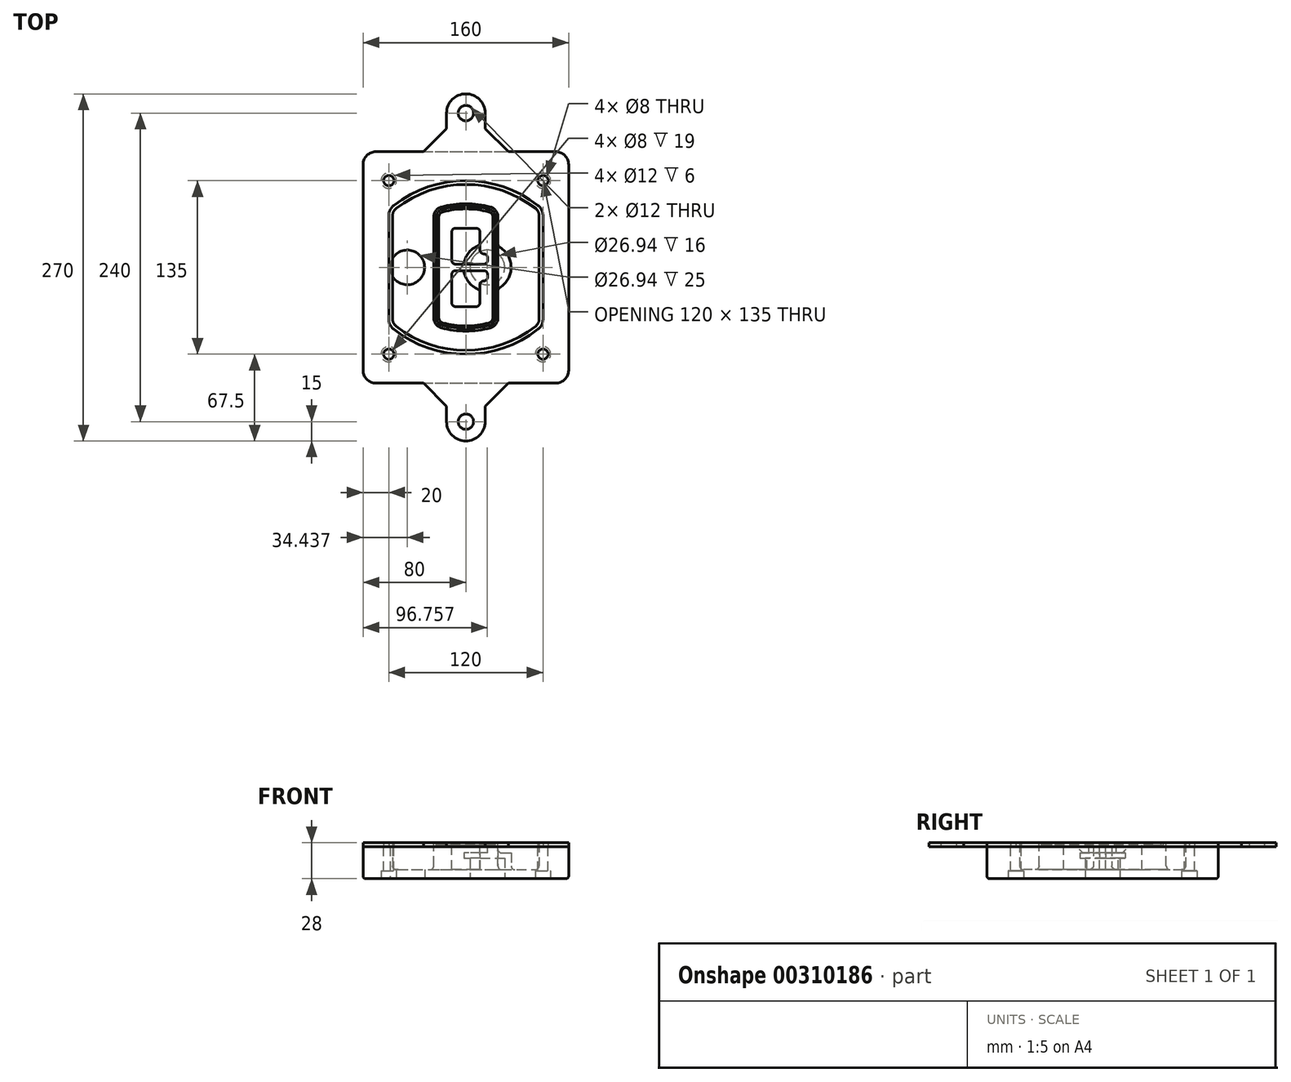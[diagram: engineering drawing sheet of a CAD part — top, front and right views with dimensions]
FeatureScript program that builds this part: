
annotation { "Feature Type Name" : "Feature", "Feature Type Description" : "" }
export const myFeature = defineFeature(function(context is Context, id is Id, definition is map)
    precondition{}
    {
        {
            var Q0;
            Q0=qCreatedBy(makeId("Top.planeOp"),FACE);
            var sketch = newSketch(context, id + "F0", { "sketchPlane" : qUnion([Q0])});
            skPoint(sketch, "E0.rect.middle", {"position": v(0, 0) * mm});
            skLineSegment(sketch, "E1.bottom", {"start": v(-70, -90) * mm, "end": v(70, -90) * mm});
            skLineSegment(sketch, "E1.top", {"start": v(-70, 90) * mm, "end": v(70, 90) * mm});
            skLineSegment(sketch, "E1.left", {"start": v(-80, -80) * mm, "end": v(-80, 80) * mm});
            skLineSegment(sketch, "E1.right", {"start": v(80, -80) * mm, "end": v(80, 80) * mm});
            skLineSegment(sketch, "E2", {"start": v(-80, 90) * mm, "end": v(80, -90) * mm, "construction": true});
            skLineSegment(sketch, "E3", {"start": v(80, 90) * mm, "end": v(-80, -90) * mm, "construction": true});
            skCircle(sketch, "E4", {"center": v(-60, 67.5) * mm, "radius": 4 * mm});
            skCircle(sketch, "E5", {"center": v(60, 67.5) * mm, "radius": 4 * mm});
            skCircle(sketch, "E6", {"center": v(60, -67.5) * mm, "radius": 4 * mm});
            skCircle(sketch, "E7", {"center": v(-60, -67.5) * mm, "radius": 4 * mm});
            skLineSegment(sketch, "E8", {"start": v(-60, 67.5) * mm, "end": v(60, 67.5) * mm, "construction": true});
            skLineSegment(sketch, "E9", {"start": v(60, 67.5) * mm, "end": v(60, -67.5) * mm, "construction": true});
            skLineSegment(sketch, "E10", {"start": v(60, -67.5) * mm, "end": v(-60, -67.5) * mm, "construction": true});
            skLineSegment(sketch, "E11", {"start": v(-60, -67.5) * mm, "end": v(-60, 67.5) * mm, "construction": true});
            skLineSegment(sketch, "E12", {"start": v(-60, 40.3) * mm, "end": v(-60, -40.3) * mm});
            skLineSegment(sketch, "E13", {"start": v(60, 40.3) * mm, "end": v(60, -40.3) * mm});
            skArc(sketch, "E14", {"start": v(56.15, 48.18) * mm, "mid": v(0, 67.5) * mm, "end": v(-56.15, 48.18) * mm});
            skArc(sketch, "E15", {"start": v(-56.15, -48.18) * mm, "mid": v(0, -67.5) * mm, "end": v(56.15, -48.18) * mm});
            skLineSegment(sketch, "E16", {"start": v(-60, 0) * mm, "end": v(60, 0) * mm, "construction": true});
            skPoint(sketch, "E17.visualSharp", {"position": v(-60, -45) * mm});
            skArc(sketch, "E17.filletArc", {"start": v(-60, -40.3) * mm, "mid": v(-58.99, -44.68) * mm, "end": v(-56.15, -48.18) * mm});
            skPoint(sketch, "E18.visualSharp", {"position": v(-60, 45) * mm});
            skArc(sketch, "E18.filletArc", {"start": v(-56.15, 48.18) * mm, "mid": v(-58.99, 44.68) * mm, "end": v(-60, 40.3) * mm});
            skPoint(sketch, "E19.visualSharp", {"position": v(60, 45) * mm});
            skArc(sketch, "E19.filletArc", {"start": v(60, 40.3) * mm, "mid": v(58.99, 44.68) * mm, "end": v(56.15, 48.18) * mm});
            skPoint(sketch, "E20.visualSharp", {"position": v(60, -45) * mm});
            skArc(sketch, "E20.filletArc", {"start": v(56.15, -48.18) * mm, "mid": v(58.99, -44.68) * mm, "end": v(60, -40.3) * mm});
            skPoint(sketch, "E21.visualSharp", {"position": v(-80, 90) * mm});
            skArc(sketch, "E21.filletArc", {"start": v(-70, 90) * mm, "mid": v(-77.07, 87.07) * mm, "end": v(-80, 80) * mm});
            skPoint(sketch, "E22.visualSharp", {"position": v(80, 90) * mm});
            skArc(sketch, "E22.filletArc", {"start": v(80, 80) * mm, "mid": v(77.07, 87.07) * mm, "end": v(70, 90) * mm});
            skPoint(sketch, "E23.visualSharp", {"position": v(80, -90) * mm});
            skArc(sketch, "E23.filletArc", {"start": v(70, -90) * mm, "mid": v(77.07, -87.07) * mm, "end": v(80, -80) * mm});
            skPoint(sketch, "E24.visualSharp", {"position": v(-80, -90) * mm});
            skArc(sketch, "E24.filletArc", {"start": v(-80, -80) * mm, "mid": v(-77.07, -87.07) * mm, "end": v(-70, -90) * mm});
            skArc(sketch, "E25.0", {"start": v(57, 40.3) * mm, "mid": v(56.3, 43.36) * mm, "end": v(54.3, 45.81) * mm});
            skLineSegment(sketch, "E25.1", {"start": v(57, 40.3) * mm, "end": v(57, -40.3) * mm});
            skArc(sketch, "E25.2", {"start": v(54.3, -45.81) * mm, "mid": v(56.3, -43.36) * mm, "end": v(57, -40.3) * mm});
            skArc(sketch, "E25.3", {"start": v(-54.3, -45.81) * mm, "mid": v(0, -64.5) * mm, "end": v(54.3, -45.81) * mm});
            skArc(sketch, "E25.4", {"start": v(-57, -40.3) * mm, "mid": v(-56.3, -43.36) * mm, "end": v(-54.3, -45.81) * mm});
            skArc(sketch, "E25.5", {"start": v(54.3, 45.81) * mm, "mid": v(0, 64.5) * mm, "end": v(-54.3, 45.81) * mm});
            skLineSegment(sketch, "E25.6", {"start": v(-57, 40.3) * mm, "end": v(-57, -40.3) * mm});
            skArc(sketch, "E25.7", {"start": v(-54.3, 45.81) * mm, "mid": v(-56.3, 43.36) * mm, "end": v(-57, 40.3) * mm});
            skArc(sketch, "E26.0", {"start": v(-58.62, 51.33) * mm, "mid": v(-62.58, 46.43) * mm, "end": v(-64, 40.3) * mm});
            skArc(sketch, "E26.1", {"start": v(58.62, 51.33) * mm, "mid": v(0, 71.5) * mm, "end": v(-58.62, 51.33) * mm});
            skArc(sketch, "E26.2", {"start": v(64, 40.3) * mm, "mid": v(62.58, 46.43) * mm, "end": v(58.62, 51.33) * mm});
            skLineSegment(sketch, "E26.3", {"start": v(64, 40.3) * mm, "end": v(64, -40.3) * mm});
            skArc(sketch, "E26.4", {"start": v(58.62, -51.33) * mm, "mid": v(62.58, -46.43) * mm, "end": v(64, -40.3) * mm});
            skLineSegment(sketch, "E26.5", {"start": v(-64, 40.3) * mm, "end": v(-64, -40.3) * mm});
            skArc(sketch, "E26.6", {"start": v(-58.62, -51.33) * mm, "mid": v(0, -71.5) * mm, "end": v(58.62, -51.33) * mm});
            skArc(sketch, "E26.7", {"start": v(-64, -40.3) * mm, "mid": v(-62.58, -46.43) * mm, "end": v(-58.62, -51.33) * mm});
            skSolve(sketch);
        }
        {
            var Q0;
            Q0=makeQuery(id+"F0.imprint","IMPRINT",FACE,{"disambiguationData":[TD([[makeQuery(id+"F0.imprint","IMPRINT",EDGE,{"derivedFrom":sQuery(id+"F0.wireOp",EDGE,"E1.bottom")}),1.0]])]});
            var Q1;
            Q1=makeQuery(id+"F0.imprint","IMPRINT",FACE,{"disambiguationData":[TD([[makeQuery(id+"F0.imprint","IMPRINT",EDGE,{"derivedFrom":sQuery(id+"F0.wireOp",EDGE,"E12")}),1.0]])]});
            var Q2;
            Q2=makeQuery(id+"F0.imprint","IMPRINT",FACE,{"disambiguationData":[TD([[makeQuery(id+"F0.imprint","IMPRINT",EDGE,{"derivedFrom":sQuery(id+"F0.wireOp",EDGE,"E25.0")}),1.0]])]});
            var Q3;
            Q3=makeQuery(id+"F0.imprint","IMPRINT",FACE,{"disambiguationData":[TD([[makeQuery(id+"F0.imprint","IMPRINT",EDGE,{"derivedFrom":sQuery(id+"F0.wireOp",EDGE,"E12")}),-1.0]])]});
            extrude(context, id + "F1", {"entities" : qUnion([Q0, Q1, Q2, Q3]), "oppositeDirection" : true, "depth" : 25 * mm});
        }
        {
            var Q0;
            Q0=makeQuery(id+"F0.imprint","IMPRINT",FACE,{"disambiguationData":[TD([[makeQuery(id+"F0.imprint","IMPRINT",EDGE,{"derivedFrom":sQuery(id+"F0.wireOp",EDGE,"E12")}),1.0]])]});
            extrude(context, id + "F2", {"entities" : qUnion([Q0]), "operationType" : NewBodyOperationType.ADD, "depth" : 3 * mm});
        }
        {
            var Q0;
            Q0=makeQuery(id+"F0.imprint","IMPRINT",FACE,{"disambiguationData":[TD([[makeQuery(id+"F0.imprint","IMPRINT",EDGE,{"derivedFrom":sQuery(id+"F0.wireOp",EDGE,"E25.0")}),1.0]])]});
            extrude(context, id + "F3", {"entities" : qUnion([Q0]), "operationType" : NewBodyOperationType.REMOVE, "oppositeDirection" : true, "depth" : 18 * mm});
        }
        {
            var Q0;
            Q0=makeQuery(id+"F2.opExtrude","CAP_FACE",FACE,{"disambiguationData":[OSD([sQuery(id+"F0.wireOp",EDGE,"E12"),sQuery(id+"F0.wireOp",EDGE,"E13"),sQuery(id+"F0.wireOp",EDGE,"E14"),sQuery(id+"F0.wireOp",EDGE,"E15"),sQuery(id+"F0.wireOp",EDGE,"E17.filletArc"),sQuery(id+"F0.wireOp",EDGE,"E18.filletArc"),sQuery(id+"F0.wireOp",EDGE,"E19.filletArc"),sQuery(id+"F0.wireOp",EDGE,"E20.filletArc"),sQuery(id+"F0.wireOp",EDGE,"E25.0"),sQuery(id+"F0.wireOp",EDGE,"E25.1"),sQuery(id+"F0.wireOp",EDGE,"E25.2"),sQuery(id+"F0.wireOp",EDGE,"E25.3"),sQuery(id+"F0.wireOp",EDGE,"E25.4"),sQuery(id+"F0.wireOp",EDGE,"E25.5"),sQuery(id+"F0.wireOp",EDGE,"E25.6"),sQuery(id+"F0.wireOp",EDGE,"E25.7")])],"isStart":false});
            var sketch = newSketch(context, id + "F4", { "sketchPlane" : qUnion([Q0])});
            skArc(sketch, "E27.0", {"start": v(-19.08, -46.97) * mm, "mid": v(0, -49.5) * mm, "end": v(19.08, -46.97) * mm});
            skArc(sketch, "E28.0", {"start": v(19.08, 46.97) * mm, "mid": v(0, 49.5) * mm, "end": v(-19.08, 46.97) * mm});
            skLineSegment(sketch, "E29", {"start": v(-25, 39.25) * mm, "end": v(-25, -39.25) * mm});
            skLineSegment(sketch, "E30", {"start": v(25, 39.25) * mm, "end": v(25, -39.25) * mm});
            skLineSegment(sketch, "E31", {"start": v(-25, 45.1) * mm, "end": v(25, 45.1) * mm, "construction": true});
            skLineSegment(sketch, "E32", {"start": v(-25, -45.1) * mm, "end": v(25, -45.1) * mm, "construction": true});
            skPoint(sketch, "E33.visualSharp", {"position": v(-25, 45.1) * mm});
            skArc(sketch, "E33.filletArc", {"start": v(-19.08, 46.97) * mm, "mid": v(-23.35, 44.11) * mm, "end": v(-25, 39.25) * mm});
            skPoint(sketch, "E34.visualSharp", {"position": v(25, 45.1) * mm});
            skArc(sketch, "E34.filletArc", {"start": v(25, 39.25) * mm, "mid": v(23.35, 44.11) * mm, "end": v(19.08, 46.97) * mm});
            skPoint(sketch, "E35.visualSharp", {"position": v(25, -45.1) * mm});
            skArc(sketch, "E35.filletArc", {"start": v(19.08, -46.97) * mm, "mid": v(23.35, -44.11) * mm, "end": v(25, -39.25) * mm});
            skPoint(sketch, "E36.visualSharp", {"position": v(-25, -45.1) * mm});
            skArc(sketch, "E36.filletArc", {"start": v(-25, -39.25) * mm, "mid": v(-23.35, -44.11) * mm, "end": v(-19.08, -46.97) * mm});
            skArc(sketch, "E37.0", {"start": v(54.3, 45.81) * mm, "mid": v(0, 64.5) * mm, "end": v(-54.3, 45.81) * mm});
            skArc(sketch, "E37.1", {"start": v(-54.3, 45.81) * mm, "mid": v(-56.3, 43.36) * mm, "end": v(-57, 40.3) * mm});
            skLineSegment(sketch, "E37.2", {"start": v(-57, 40.3) * mm, "end": v(-57, -40.3) * mm});
            skArc(sketch, "E37.3", {"start": v(-57, -40.3) * mm, "mid": v(-56.3, -43.36) * mm, "end": v(-54.3, -45.81) * mm});
            skArc(sketch, "E37.4", {"start": v(-54.3, -45.81) * mm, "mid": v(0, -64.5) * mm, "end": v(54.3, -45.81) * mm});
            skArc(sketch, "E37.5", {"start": v(54.3, -45.81) * mm, "mid": v(56.3, -43.36) * mm, "end": v(57, -40.3) * mm});
            skLineSegment(sketch, "E37.6", {"start": v(57, 40.3) * mm, "end": v(57, -40.3) * mm});
            skArc(sketch, "E37.7", {"start": v(57, 40.3) * mm, "mid": v(56.3, 43.36) * mm, "end": v(54.3, 45.81) * mm});
            skLineSegment(sketch, "E38.0", {"start": v(23, 39.25) * mm, "end": v(23, -39.25) * mm});
            skArc(sketch, "E38.1", {"start": v(18.56, -45.04) * mm, "mid": v(21.76, -42.9) * mm, "end": v(23, -39.25) * mm});
            skArc(sketch, "E38.2", {"start": v(-18.56, -45.04) * mm, "mid": v(0, -47.5) * mm, "end": v(18.56, -45.04) * mm});
            skArc(sketch, "E38.3", {"start": v(-23, -39.25) * mm, "mid": v(-21.76, -42.9) * mm, "end": v(-18.56, -45.04) * mm});
            skLineSegment(sketch, "E38.4", {"start": v(-23, 39.25) * mm, "end": v(-23, -39.25) * mm});
            skArc(sketch, "E38.5", {"start": v(23, 39.25) * mm, "mid": v(21.76, 42.9) * mm, "end": v(18.56, 45.04) * mm});
            skArc(sketch, "E38.6", {"start": v(-18.56, 45.04) * mm, "mid": v(-21.76, 42.9) * mm, "end": v(-23, 39.25) * mm});
            skArc(sketch, "E38.7", {"start": v(18.56, 45.04) * mm, "mid": v(0, 47.5) * mm, "end": v(-18.56, 45.04) * mm});
            skArc(sketch, "E39.0", {"start": v(21, 39.25) * mm, "mid": v(20.18, 41.68) * mm, "end": v(18.04, 43.1) * mm});
            skLineSegment(sketch, "E39.1", {"start": v(21, 39.25) * mm, "end": v(21, -39.25) * mm});
            skArc(sketch, "E39.2", {"start": v(18.04, -43.1) * mm, "mid": v(20.18, -41.68) * mm, "end": v(21, -39.25) * mm});
            skArc(sketch, "E39.3", {"start": v(-18.04, -43.1) * mm, "mid": v(0, -45.5) * mm, "end": v(18.04, -43.1) * mm});
            skArc(sketch, "E39.4", {"start": v(-21, -39.25) * mm, "mid": v(-20.18, -41.68) * mm, "end": v(-18.04, -43.1) * mm});
            skArc(sketch, "E39.5", {"start": v(18.04, 43.1) * mm, "mid": v(0, 45.5) * mm, "end": v(-18.04, 43.1) * mm});
            skLineSegment(sketch, "E39.6", {"start": v(-21, 39.25) * mm, "end": v(-21, -39.25) * mm});
            skArc(sketch, "E39.7", {"start": v(-18.04, 43.1) * mm, "mid": v(-20.18, 41.68) * mm, "end": v(-21, 39.25) * mm});
            skLineSegment(sketch, "E40", {"start": v(-25, 0) * mm, "end": v(25, 0) * mm, "construction": true});
            skLineSegment(sketch, "E41", {"start": v(-11, 5.5) * mm, "end": v(-11, 27.5) * mm});
            skLineSegment(sketch, "E42", {"start": v(-8, 30.5) * mm, "end": v(8, 30.5) * mm});
            skLineSegment(sketch, "E43", {"start": v(11, 27.5) * mm, "end": v(11, 13.5) * mm});
            skLineSegment(sketch, "E44", {"start": v(14, 10.5) * mm, "end": v(14, 10.5) * mm});
            skLineSegment(sketch, "E45", {"start": v(17, 7.5) * mm, "end": v(17, 5.5) * mm});
            skLineSegment(sketch, "E46", {"start": v(14, 2.5) * mm, "end": v(-8, 2.5) * mm});
            skPoint(sketch, "E47.visualSharp", {"position": v(-11, 30.5) * mm});
            skArc(sketch, "E47.filletArc", {"start": v(-8, 30.5) * mm, "mid": v(-10.12, 29.62) * mm, "end": v(-11, 27.5) * mm});
            skPoint(sketch, "E48.visualSharp", {"position": v(11, 30.5) * mm});
            skArc(sketch, "E48.filletArc", {"start": v(11, 27.5) * mm, "mid": v(10.12, 29.62) * mm, "end": v(8, 30.5) * mm});
            skPoint(sketch, "E49.visualSharp", {"position": v(11, 10.5) * mm});
            skArc(sketch, "E49.filletArc", {"start": v(11, 13.5) * mm, "mid": v(11.88, 11.38) * mm, "end": v(14, 10.5) * mm});
            skPoint(sketch, "E50.visualSharp", {"position": v(17, 10.5) * mm});
            skArc(sketch, "E50.filletArc", {"start": v(17, 7.5) * mm, "mid": v(16.12, 9.62) * mm, "end": v(14, 10.5) * mm});
            skPoint(sketch, "E51.visualSharp", {"position": v(17, 2.5) * mm});
            skArc(sketch, "E51.filletArc", {"start": v(14, 2.5) * mm, "mid": v(16.12, 3.38) * mm, "end": v(17, 5.5) * mm});
            skPoint(sketch, "E52.visualSharp", {"position": v(-11, 2.5) * mm});
            skArc(sketch, "E52.filletArc", {"start": v(-11, 5.5) * mm, "mid": v(-10.12, 3.38) * mm, "end": v(-8, 2.5) * mm});
            skLineSegment(sketch, "E53.0.MirrorCS", {"start": v(14, -2.5) * mm, "end": v(-8, -2.5) * mm});
            skArc(sketch, "E54.0.MirrorCS", {"start": v(-11, -5.5) * mm, "mid": v(-10.12, -3.38) * mm, "end": v(-8, -2.5) * mm});
            skLineSegment(sketch, "E55.0.MirrorCS", {"start": v(-11, -5.5) * mm, "end": v(-11, -27.5) * mm});
            skArc(sketch, "E56.0.MirrorCS", {"start": v(-8, -30.5) * mm, "mid": v(-10.12, -29.62) * mm, "end": v(-11, -27.5) * mm});
            skLineSegment(sketch, "E57.0.MirrorCS", {"start": v(-8, -30.5) * mm, "end": v(8, -30.5) * mm});
            skArc(sketch, "E58.0.MirrorCS", {"start": v(11, -27.5) * mm, "mid": v(10.12, -29.62) * mm, "end": v(8, -30.5) * mm});
            skLineSegment(sketch, "E59.0.MirrorCS", {"start": v(11, -27.5) * mm, "end": v(11, -13.5) * mm});
            skArc(sketch, "E60.0.MirrorCS", {"start": v(11, -13.5) * mm, "mid": v(11.88, -11.38) * mm, "end": v(14, -10.5) * mm});
            skArc(sketch, "E61.0.MirrorCS", {"start": v(17, -7.5) * mm, "mid": v(16.12, -9.62) * mm, "end": v(14, -10.5) * mm});
            skLineSegment(sketch, "E62.0.MirrorCS", {"start": v(17, -7.5) * mm, "end": v(17, -5.5) * mm});
            skArc(sketch, "E63.0.MirrorCS", {"start": v(14, -2.5) * mm, "mid": v(16.12, -3.38) * mm, "end": v(17, -5.5) * mm});
            skSolve(sketch);
        }
        {
            var Q0;
            Q0=makeQuery(id+"F4.imprint","IMPRINT",FACE,{"disambiguationData":[TD([[makeQuery(id+"F4.imprint","IMPRINT",EDGE,{"derivedFrom":sQuery(id+"F4.wireOp",EDGE,"E27.0")}),1.0]])]});
            var Q1;
            Q1=makeQuery(id+"F4.imprint","IMPRINT",FACE,{"disambiguationData":[TD([[makeQuery(id+"F4.imprint","IMPRINT",EDGE,{"derivedFrom":sQuery(id+"F4.wireOp",EDGE,"E38.0")}),-1.0]])]});
            var Q2;
            Q2=makeQuery(id+"F4.imprint","IMPRINT",FACE,{"disambiguationData":[TD([[makeQuery(id+"F4.imprint","IMPRINT",EDGE,{"derivedFrom":sQuery(id+"F4.wireOp",EDGE,"E39.0")}),1.0]])]});
            extrude(context, id + "F5", {"entities" : qUnion([Q0, Q1, Q2]), "operationType" : NewBodyOperationType.ADD, "endBound" : BoundingType.UP_TO_NEXT, "oppositeDirection" : true, "depth" : 25 * mm});
        }
        {
            var Q0;
            Q0=makeQuery(id+"F4.imprint","IMPRINT",FACE,{"disambiguationData":[TD([[makeQuery(id+"F4.imprint","IMPRINT",EDGE,{"derivedFrom":sQuery(id+"F4.wireOp",EDGE,"E38.0")}),-1.0]])]});
            extrude(context, id + "F6", {"entities" : qUnion([Q0]), "operationType" : NewBodyOperationType.REMOVE, "oppositeDirection" : true, "depth" : 2 * mm});
        }
        {
            var Q0;
            Q0=makeQuery(id+"F1.opExtrude","CAP_FACE",FACE,{"disambiguationData":[OSD([sQuery(id+"F0.wireOp",EDGE,"E1.bottom"),sQuery(id+"F0.wireOp",EDGE,"E1.top"),sQuery(id+"F0.wireOp",EDGE,"E1.left"),sQuery(id+"F0.wireOp",EDGE,"E1.right"),sQuery(id+"F0.wireOp",EDGE,"E4"),sQuery(id+"F0.wireOp",EDGE,"E5"),sQuery(id+"F0.wireOp",EDGE,"E6"),sQuery(id+"F0.wireOp",EDGE,"E7"),sQuery(id+"F0.wireOp",EDGE,"E21.filletArc"),sQuery(id+"F0.wireOp",EDGE,"E22.filletArc"),sQuery(id+"F0.wireOp",EDGE,"E23.filletArc"),sQuery(id+"F0.wireOp",EDGE,"E24.filletArc")])],"isStart":false});
            var sketch = newSketch(context, id + "F7", { "sketchPlane" : qUnion([Q0])});
            skCircle(sketch, "E64", {"center": v(16.76, 0) * mm, "radius": 13.47 * mm});
            skCircle(sketch, "E65", {"center": v(-45.56, 0) * mm, "radius": 13.47 * mm});
            skLineSegment(sketch, "E66", {"start": v(80, 0) * mm, "end": v(-80, 0) * mm});
            skCircle(sketch, "E67", {"center": v(16.76, 0) * mm, "radius": 18.47 * mm});
            skCircle(sketch, "E68", {"center": v(60, -67.5) * mm, "radius": 6 * mm});
            skCircle(sketch, "E69", {"center": v(-60, -67.5) * mm, "radius": 6 * mm});
            skCircle(sketch, "E70", {"center": v(-60, 67.5) * mm, "radius": 6 * mm});
            skCircle(sketch, "E71", {"center": v(60, 67.5) * mm, "radius": 6 * mm});
            skSolve(sketch);
        }
        {
            var Q0;
            {var subQ1=sQuery(id+"F7.wireOp",EDGE,"E66");var subQ4=sQuery(id+"F7.wireOp",EDGE,"E64");var subQ6=makeQuery(id+"F7.imprint","INTERSECT",VERTEX,{"disambiguationData":[OD(0.0)],"derivedFrom":[subQ4,subQ1]});Q0=makeQuery(id+"F7.imprint","IMPRINT",FACE,{"disambiguationData":[TD([[makeQuery(id+"F7.imprint","IMPRINT",EDGE,{"disambiguationData":[TD([[subQ6,-1.0]])],"derivedFrom":subQ4}),-1.0]])]});}
            var Q1;
            {var subQ0=sQuery(id+"F7.wireOp",EDGE,"E66");var subQ1=sQuery(id+"F7.wireOp",EDGE,"E64");var subQ3=makeQuery(id+"F7.imprint","INTERSECT",VERTEX,{"disambiguationData":[OD(0.0)],"derivedFrom":[subQ1,subQ0]});Q1=makeQuery(id+"F7.imprint","IMPRINT",FACE,{"disambiguationData":[TD([[makeQuery(id+"F7.imprint","IMPRINT",EDGE,{"disambiguationData":[TD([[subQ3,-1.0]])],"derivedFrom":subQ1}),1.0]])]});}
            var Q2;
            {var subQ0=sQuery(id+"F7.wireOp",EDGE,"E66");var subQ1=sQuery(id+"F7.wireOp",EDGE,"E64");var subQ3=makeQuery(id+"F7.imprint","INTERSECT",VERTEX,{"disambiguationData":[OD(0.0)],"derivedFrom":[subQ1,subQ0]});Q2=makeQuery(id+"F7.imprint","IMPRINT",FACE,{"disambiguationData":[TD([[makeQuery(id+"F7.imprint","IMPRINT",EDGE,{"disambiguationData":[TD([[subQ3,1.0]])],"derivedFrom":subQ1}),1.0]])]});}
            var Q3;
            {var subQ1=sQuery(id+"F7.wireOp",EDGE,"E66");var subQ4=sQuery(id+"F7.wireOp",EDGE,"E64");var subQ6=makeQuery(id+"F7.imprint","INTERSECT",VERTEX,{"disambiguationData":[OD(0.0)],"derivedFrom":[subQ4,subQ1]});Q3=makeQuery(id+"F7.imprint","IMPRINT",FACE,{"disambiguationData":[TD([[makeQuery(id+"F7.imprint","IMPRINT",EDGE,{"disambiguationData":[TD([[subQ6,1.0]])],"derivedFrom":subQ4}),-1.0]])]});}
            extrude(context, id + "F8", {"entities" : qUnion([Q0, Q1, Q2, Q3]), "operationType" : NewBodyOperationType.ADD, "oppositeDirection" : true, "depth" : 20 * mm});
        }
        {
            var Q0;
            {var subQ0=sQuery(id+"F7.wireOp",EDGE,"E66");var subQ1=sQuery(id+"F7.wireOp",EDGE,"E64");var subQ3=makeQuery(id+"F7.imprint","INTERSECT",VERTEX,{"disambiguationData":[OD(0.0)],"derivedFrom":[subQ1,subQ0]});Q0=makeQuery(id+"F7.imprint","IMPRINT",FACE,{"disambiguationData":[TD([[makeQuery(id+"F7.imprint","IMPRINT",EDGE,{"disambiguationData":[TD([[subQ3,-1.0]])],"derivedFrom":subQ1}),1.0]])]});}
            var Q1;
            {var subQ0=sQuery(id+"F7.wireOp",EDGE,"E66");var subQ1=sQuery(id+"F7.wireOp",EDGE,"E64");var subQ3=makeQuery(id+"F7.imprint","INTERSECT",VERTEX,{"disambiguationData":[OD(0.0)],"derivedFrom":[subQ1,subQ0]});Q1=makeQuery(id+"F7.imprint","IMPRINT",FACE,{"disambiguationData":[TD([[makeQuery(id+"F7.imprint","IMPRINT",EDGE,{"disambiguationData":[TD([[subQ3,1.0]])],"derivedFrom":subQ1}),1.0]])]});}
            extrude(context, id + "F9", {"entities" : qUnion([Q0, Q1]), "operationType" : NewBodyOperationType.REMOVE, "oppositeDirection" : true, "depth" : 16 * mm});
        }
        {
            var Q0;
            {var subQ0=sQuery(id+"F7.wireOp",EDGE,"E66");var subQ1=sQuery(id+"F7.wireOp",EDGE,"E65");var subQ3=makeQuery(id+"F7.imprint","INTERSECT",VERTEX,{"disambiguationData":[OD(0.0)],"derivedFrom":[subQ1,subQ0]});Q0=makeQuery(id+"F7.imprint","IMPRINT",FACE,{"disambiguationData":[TD([[makeQuery(id+"F7.imprint","IMPRINT",EDGE,{"disambiguationData":[TD([[subQ3,-1.0]])],"derivedFrom":subQ1}),1.0]])]});}
            var Q1;
            {var subQ0=sQuery(id+"F7.wireOp",EDGE,"E66");var subQ1=sQuery(id+"F7.wireOp",EDGE,"E65");var subQ3=makeQuery(id+"F7.imprint","INTERSECT",VERTEX,{"disambiguationData":[OD(0.0)],"derivedFrom":[subQ1,subQ0]});Q1=makeQuery(id+"F7.imprint","IMPRINT",FACE,{"disambiguationData":[TD([[makeQuery(id+"F7.imprint","IMPRINT",EDGE,{"disambiguationData":[TD([[subQ3,1.0]])],"derivedFrom":subQ1}),1.0]])]});}
            extrude(context, id + "F10", {"entities" : qUnion([Q0, Q1]), "operationType" : NewBodyOperationType.REMOVE, "oppositeDirection" : true, "depth" : 25 * mm});
        }
        {
            var Q0;
            Q0=makeQuery(id+"F7.imprint","IMPRINT",FACE,{"disambiguationData":[TD([[makeQuery(id+"F7.imprint","IMPRINT",EDGE,{"derivedFrom":sQuery(id+"F7.wireOp",EDGE,"E68")}),1.0]])]});
            var Q1;
            Q1=makeQuery(id+"F7.imprint","IMPRINT",FACE,{"disambiguationData":[TD([[makeQuery(id+"F7.imprint","IMPRINT",EDGE,{"derivedFrom":makeQuery(id+"F1.opExtrude","CAP_EDGE",EDGE,{"disambiguationData":[OSD([sQuery(id+"F0.wireOp",EDGE,"E5")])],"isStart":false})}),-1.0]])]});
            var Q2;
            Q2=makeQuery(id+"F7.imprint","IMPRINT",FACE,{"disambiguationData":[TD([[makeQuery(id+"F7.imprint","IMPRINT",EDGE,{"derivedFrom":sQuery(id+"F7.wireOp",EDGE,"E69")}),1.0]])]});
            var Q3;
            Q3=makeQuery(id+"F7.imprint","IMPRINT",FACE,{"disambiguationData":[TD([[makeQuery(id+"F7.imprint","IMPRINT",EDGE,{"derivedFrom":makeQuery(id+"F1.opExtrude","CAP_EDGE",EDGE,{"disambiguationData":[OSD([sQuery(id+"F0.wireOp",EDGE,"E4")])],"isStart":false})}),-1.0]])]});
            var Q4;
            Q4=makeQuery(id+"F7.imprint","IMPRINT",FACE,{"disambiguationData":[TD([[makeQuery(id+"F7.imprint","IMPRINT",EDGE,{"derivedFrom":sQuery(id+"F7.wireOp",EDGE,"E70")}),1.0]])]});
            var Q5;
            Q5=makeQuery(id+"F7.imprint","IMPRINT",FACE,{"disambiguationData":[TD([[makeQuery(id+"F7.imprint","IMPRINT",EDGE,{"derivedFrom":makeQuery(id+"F1.opExtrude","CAP_EDGE",EDGE,{"disambiguationData":[OSD([sQuery(id+"F0.wireOp",EDGE,"E7")])],"isStart":false})}),-1.0]])]});
            var Q6;
            Q6=makeQuery(id+"F7.imprint","IMPRINT",FACE,{"disambiguationData":[TD([[makeQuery(id+"F7.imprint","IMPRINT",EDGE,{"derivedFrom":sQuery(id+"F7.wireOp",EDGE,"E71")}),1.0]])]});
            var Q7;
            Q7=makeQuery(id+"F7.imprint","IMPRINT",FACE,{"disambiguationData":[TD([[makeQuery(id+"F7.imprint","IMPRINT",EDGE,{"derivedFrom":makeQuery(id+"F1.opExtrude","CAP_EDGE",EDGE,{"disambiguationData":[OSD([sQuery(id+"F0.wireOp",EDGE,"E6")])],"isStart":false})}),-1.0]])]});
            extrude(context, id + "F11", {"entities" : qUnion([Q0, Q1, Q2, Q3, Q4, Q5, Q6, Q7]), "operationType" : NewBodyOperationType.REMOVE, "oppositeDirection" : true, "depth" : 6 * mm});
        }
        {
            var Q0;
            Q0=makeQuery(id+"F9.boolean.opBoolean","COPY",FACE,{"derivedFrom":makeQuery(id+"F9.opExtrude","CAP_FACE",FACE,{"disambiguationData":[OSD([sQuery(id+"F7.wireOp",EDGE,"E64")])],"isStart":false})});
            var sketch = newSketch(context, id + "F12", { "sketchPlane" : qUnion([Q0])});
            skArc(sketch, "E72.0", {"start": v(11, 17.55) * mm, "mid": v(2.57, 11.82) * mm, "end": v(-1.54, 2.5) * mm});
            skArc(sketch, "E72.1", {"start": v(-1.54, -2.5) * mm, "mid": v(2.57, -11.82) * mm, "end": v(11, -17.55) * mm});
            skLineSegment(sketch, "E73", {"start": v(-1.54, -2.5) * mm, "end": v(14, -2.5) * mm});
            skLineSegment(sketch, "E74.0", {"start": v(14, 2.5) * mm, "end": v(-1.54, 2.5) * mm});
            skArc(sketch, "E74.1", {"start": v(14, 2.5) * mm, "mid": v(16.12, 3.38) * mm, "end": v(17, 5.5) * mm});
            skLineSegment(sketch, "E74.2", {"start": v(17, 7.5) * mm, "end": v(17, 5.5) * mm});
            skArc(sketch, "E74.3", {"start": v(17, 7.5) * mm, "mid": v(16.12, 9.62) * mm, "end": v(14, 10.5) * mm});
            skArc(sketch, "E74.4", {"start": v(11, 13.5) * mm, "mid": v(11.88, 11.38) * mm, "end": v(14, 10.5) * mm});
            skLineSegment(sketch, "E74.5", {"start": v(11, 17.55) * mm, "end": v(11, 13.5) * mm});
            skLineSegment(sketch, "E74.7", {"start": v(14, -2.5) * mm, "end": v(-1.54, -2.5) * mm});
            skArc(sketch, "E74.8", {"start": v(14, -2.5) * mm, "mid": v(16.12, -3.38) * mm, "end": v(17, -5.5) * mm});
            skLineSegment(sketch, "E74.9", {"start": v(17, -7.5) * mm, "end": v(17, -5.5) * mm});
            skArc(sketch, "E74.10", {"start": v(17, -7.5) * mm, "mid": v(16.12, -9.62) * mm, "end": v(14, -10.5) * mm});
            skArc(sketch, "E74.11", {"start": v(11, -13.5) * mm, "mid": v(11.88, -11.38) * mm, "end": v(14, -10.5) * mm});
            skLineSegment(sketch, "E74.12", {"start": v(11, -17.55) * mm, "end": v(11, -13.5) * mm});
            skPoint(sketch, "E75.orphan", {"position": v(11, -27.5) * mm});
            skPoint(sketch, "E76.orphan", {"position": v(-8, -2.5) * mm});
            skPoint(sketch, "E77.orphan", {"position": v(-8, 2.5) * mm});
            skPoint(sketch, "E78.orphan", {"position": v(11, 27.5) * mm});
            skSolve(sketch);
        }
        {
            var Q0;
            {var subQ7=sQuery(id+"F12.wireOp",EDGE,"E72.0");var subQ14=sQuery(id+"F12.wireOp",EDGE,"E72.1");var subQ16=sQuery(id+"F12.wireOp",EDGE,"E74.1");var subQ18=sQuery(id+"F12.wireOp",EDGE,"E74.8");Q0=qUnion([makeQuery(id+"F12.imprint","IMPRINT",FACE,{"disambiguationData":[TD([[makeQuery(id+"F12.imprint","IMPRINT",EDGE,{"derivedFrom":subQ7}),1.0]])]}),makeQuery(id+"F12.imprint","IMPRINT",FACE,{"disambiguationData":[TD([[makeQuery(id+"F12.imprint","IMPRINT",EDGE,{"derivedFrom":subQ14}),1.0]])]}),makeQuery(id+"F12.imprint","IMPRINT",FACE,{"disambiguationData":[TD([[makeQuery(id+"F12.imprint","IMPRINT",EDGE,{"derivedFrom":subQ16}),1.0]])]}),makeQuery(id+"F12.imprint","IMPRINT",FACE,{"disambiguationData":[TD([[makeQuery(id+"F12.imprint","IMPRINT",EDGE,{"derivedFrom":subQ18}),-1.0]])]})]);}
            var Q1;
            Q1=makeQuery(id+"F5.boolean.opBoolean","SPLIT",FACE,{"disambiguationData":[TD([makeQuery(id+"F5.opExtrude","SWEPT_FACE",FACE,{"disambiguationData":[OSD([sQuery(id+"F4.wireOp",EDGE,"E41")])]})])],"derivedFrom":makeQuery(id+"F3.boolean.opBoolean","COPY",FACE,{"derivedFrom":makeQuery(id+"F3.opExtrude","CAP_FACE",FACE,{"disambiguationData":[OSD([sQuery(id+"F0.wireOp",EDGE,"E25.0"),sQuery(id+"F0.wireOp",EDGE,"E25.1"),sQuery(id+"F0.wireOp",EDGE,"E25.2"),sQuery(id+"F0.wireOp",EDGE,"E25.3"),sQuery(id+"F0.wireOp",EDGE,"E25.4"),sQuery(id+"F0.wireOp",EDGE,"E25.5"),sQuery(id+"F0.wireOp",EDGE,"E25.6"),sQuery(id+"F0.wireOp",EDGE,"E25.7")])],"isStart":false})})});
            extrude(context, id + "F13", {"entities" : qUnion([Q0]), "operationType" : NewBodyOperationType.REMOVE, "endBound" : BoundingType.UP_TO_SURFACE, "endBoundEntityFace" : qUnion([Q1]), "depth" : 25 * mm});
        }
        {
            var Q0;
            Q0=makeQuery(id+"F3.boolean.opBoolean","COPY",EDGE,{"derivedFrom":makeQuery(id+"F3.opExtrude","CAP_EDGE",EDGE,{"disambiguationData":[OSD([sQuery(id+"F0.wireOp",EDGE,"E25.6")])],"isStart":false})});
            var Q1;
            Q1=makeQuery(id+"F8.boolean.opBoolean","INTERSECT",EDGE,{"derivedFrom":[makeQuery(id+"F5.opExtrude","SWEPT_FACE",FACE,{"disambiguationData":[OSD([sQuery(id+"F4.wireOp",EDGE,"E30")])]}),makeQuery(id+"F8.opExtrude","CAP_FACE",FACE,{"disambiguationData":[OSD([sQuery(id+"F7.wireOp",EDGE,"E67")])],"isStart":false})]});
            var Q2;
            Q2=makeQuery(id+"F8.boolean.opBoolean","INTERSECT",EDGE,{"disambiguationData":[OD(1.0)],"derivedFrom":[makeQuery(id+"F5.opExtrude","SWEPT_FACE",FACE,{"disambiguationData":[OSD([sQuery(id+"F4.wireOp",EDGE,"E30")])]}),makeQuery(id+"F8.opExtrude","SWEPT_FACE",FACE,{"disambiguationData":[OSD([sQuery(id+"F7.wireOp",EDGE,"E67")])]})]});
            var Q3;
            {var subQ0=sQuery(id+"F4.wireOp",EDGE,"E30");Q3=makeQuery(id+"F8.boolean.opBoolean","SPLIT",EDGE,{"disambiguationData":[TD([makeQuery(id+"F5.opExtrude","SWEPT_FACE",FACE,{"disambiguationData":[OSD([sQuery(id+"F4.wireOp",EDGE,"E35.filletArc")])]})])],"derivedFrom":makeQuery(id+"F5.opExtrude","CAP_EDGE",EDGE,{"disambiguationData":[OSD([subQ0])],"isStart":false})});}
            var Q4;
            {var subQ0=sQuery(id+"F0.wireOp",EDGE,"E25.7");var subQ1=sQuery(id+"F0.wireOp",EDGE,"E25.1");var subQ2=sQuery(id+"F0.wireOp",EDGE,"E25.6");var subQ3=sQuery(id+"F0.wireOp",EDGE,"E25.5");var subQ4=sQuery(id+"F0.wireOp",EDGE,"E25.4");var subQ5=sQuery(id+"F0.wireOp",EDGE,"E25.0");var subQ6=sQuery(id+"F0.wireOp",EDGE,"E25.2");var subQ7=sQuery(id+"F0.wireOp",EDGE,"E25.3");Q4=makeQuery(id+"F8.boolean.opBoolean","INTERSECT",EDGE,{"derivedFrom":[makeQuery(id+"F5.boolean.opBoolean","SPLIT",FACE,{"disambiguationData":[TD([makeQuery(id+"F2.opExtrude","SWEPT_FACE",FACE,{"disambiguationData":[OSD([subQ5])]})])],"derivedFrom":makeQuery(id+"F3.boolean.opBoolean","COPY",FACE,{"derivedFrom":makeQuery(id+"F3.opExtrude","CAP_FACE",FACE,{"disambiguationData":[OSD([subQ5,subQ1,subQ6,subQ7,subQ4,subQ3,subQ2,subQ0])],"isStart":false})})}),makeQuery(id+"F8.opExtrude","SWEPT_FACE",FACE,{"disambiguationData":[OSD([sQuery(id+"F7.wireOp",EDGE,"E67")])]})]});}
            var Q5;
            Q5=makeQuery(id+"F8.boolean.opBoolean","INTERSECT",EDGE,{"disambiguationData":[OD(0.0)],"derivedFrom":[makeQuery(id+"F5.opExtrude","SWEPT_FACE",FACE,{"disambiguationData":[OSD([sQuery(id+"F4.wireOp",EDGE,"E30")])]}),makeQuery(id+"F8.opExtrude","SWEPT_FACE",FACE,{"disambiguationData":[OSD([sQuery(id+"F7.wireOp",EDGE,"E67")])]})]});
            fillet(context, id + "F14", {"entities" : qUnion([Q0, Q1, Q2, Q3, Q4, Q5]), "radius" : 3 * mm, "tangentPropagation" : true, "allowEdgeOverflow" : false});
        }
        {
            var Q0;
            Q0=makeQuery(id+"F1.opExtrude","CAP_EDGE",EDGE,{"disambiguationData":[OSD([sQuery(id+"F0.wireOp",EDGE,"E1.bottom")])],"isStart":false});
            fillet(context, id + "F15", {"entities" : qUnion([Q0]), "radius" : 2 * mm, "tangentPropagation" : true, "allowEdgeOverflow" : false});
        }
        {
            var Q0;
            {var subQ0=sQuery(id+"F0.wireOp",EDGE,"E21.filletArc");var subQ1=sQuery(id+"F0.wireOp",EDGE,"E7");var subQ2=sQuery(id+"F0.wireOp",EDGE,"E6");var subQ3=sQuery(id+"F0.wireOp",EDGE,"E5");var subQ4=sQuery(id+"F0.wireOp",EDGE,"E4");var subQ5=sQuery(id+"F0.wireOp",EDGE,"E22.filletArc");var subQ6=sQuery(id+"F0.wireOp",EDGE,"E1.bottom");var subQ7=sQuery(id+"F0.wireOp",EDGE,"E1.right");var subQ8=sQuery(id+"F0.wireOp",EDGE,"E1.top");var subQ9=sQuery(id+"F0.wireOp",EDGE,"E1.left");var subQ10=sQuery(id+"F0.wireOp",EDGE,"E23.filletArc");var subQ11=sQuery(id+"F0.wireOp",EDGE,"E24.filletArc");Q0=makeQuery(id+"F2.boolean.opBoolean","SPLIT",FACE,{"disambiguationData":[TD([makeQuery(id+"F1.opExtrude","SWEPT_FACE",FACE,{"disambiguationData":[OSD([subQ6])]})])],"derivedFrom":makeQuery(id+"F1.opExtrude","CAP_FACE",FACE,{"disambiguationData":[OSD([subQ6,subQ8,subQ9,subQ7,subQ4,subQ3,subQ2,subQ1,subQ0,subQ5,subQ10,subQ11])],"isStart":true})});}
            var sketch = newSketch(context, id + "F16", { "sketchPlane" : qUnion([Q0])});
            skLineSegment(sketch, "E79.0", {"start": v(-80, -80) * mm, "end": v(-80, 80) * mm});
            skArc(sketch, "E79.1", {"start": v(-70, 90) * mm, "mid": v(-77.07, 87.07) * mm, "end": v(-80, 80) * mm});
            skLineSegment(sketch, "E79.2", {"start": v(-70, 90) * mm, "end": v(70, 90) * mm});
            skArc(sketch, "E79.3", {"start": v(80, 80) * mm, "mid": v(77.07, 87.07) * mm, "end": v(70, 90) * mm});
            skLineSegment(sketch, "E79.4", {"start": v(80, -80) * mm, "end": v(80, 80) * mm});
            skArc(sketch, "E79.5", {"start": v(70, -90) * mm, "mid": v(77.07, -87.07) * mm, "end": v(80, -80) * mm});
            skCircle(sketch, "E79.6", {"center": v(60, -67.5) * mm, "radius": 4 * mm});
            skCircle(sketch, "E79.7", {"center": v(60, 67.5) * mm, "radius": 4 * mm});
            skCircle(sketch, "E79.8", {"center": v(-60, 67.5) * mm, "radius": 4 * mm});
            skCircle(sketch, "E79.9", {"center": v(-60, -67.5) * mm, "radius": 4 * mm});
            skLineSegment(sketch, "E79.10", {"start": v(-70, -90) * mm, "end": v(70, -90) * mm});
            skArc(sketch, "E79.11", {"start": v(-80, -80) * mm, "mid": v(-77.07, -87.07) * mm, "end": v(-70, -90) * mm});
            skArc(sketch, "E79.12", {"start": v(-56.15, -48.18) * mm, "mid": v(0, -67.5) * mm, "end": v(56.15, -48.18) * mm});
            skArc(sketch, "E79.13", {"start": v(-60, -40.3) * mm, "mid": v(-58.99, -44.68) * mm, "end": v(-56.15, -48.18) * mm});
            skLineSegment(sketch, "E79.14", {"start": v(-60, 40.3) * mm, "end": v(-60, -40.3) * mm});
            skLineSegment(sketch, "E79.15", {"start": v(60, 40.3) * mm, "end": v(60, -40.3) * mm});
            skArc(sketch, "E79.16", {"start": v(56.15, -48.18) * mm, "mid": v(58.99, -44.68) * mm, "end": v(60, -40.3) * mm});
            skArc(sketch, "E79.17", {"start": v(60, 40.3) * mm, "mid": v(58.99, 44.68) * mm, "end": v(56.15, 48.18) * mm});
            skArc(sketch, "E79.18", {"start": v(56.15, 48.18) * mm, "mid": v(0, 67.5) * mm, "end": v(-56.15, 48.18) * mm});
            skArc(sketch, "E79.19", {"start": v(-56.15, 48.18) * mm, "mid": v(-58.99, 44.68) * mm, "end": v(-60, 40.3) * mm});
            skLineSegment(sketch, "E80", {"start": v(0, 90) * mm, "end": v(0, 120) * mm, "construction": true});
            skLineSegment(sketch, "E81", {"start": v(-33, 90) * mm, "end": v(-15, 108) * mm});
            skLineSegment(sketch, "E82", {"start": v(-15, 108) * mm, "end": v(-15, 120) * mm});
            skLineSegment(sketch, "E83", {"start": v(33, 90) * mm, "end": v(15, 108) * mm});
            skLineSegment(sketch, "E84", {"start": v(15, 108) * mm, "end": v(15, 120) * mm});
            skCircle(sketch, "E85", {"center": v(0, 120) * mm, "radius": 6 * mm});
            skArc(sketch, "E86", {"start": v(15, 120) * mm, "mid": v(0, 135) * mm, "end": v(-15, 120) * mm});
            skLineSegment(sketch, "E87", {"start": v(-80, 0) * mm, "end": v(80, 0) * mm, "construction": true});
            skArc(sketch, "E88.MirrorCS", {"start": v(15, -120) * mm, "mid": v(0, -135) * mm, "end": v(-15, -120) * mm});
            skCircle(sketch, "E89.MirrorC", {"center": v(0, -120) * mm, "radius": 6 * mm});
            skLineSegment(sketch, "E90.MirrorCS", {"start": v(0, -90) * mm, "end": v(0, -120) * mm, "construction": true});
            skLineSegment(sketch, "E91.MirrorCS", {"start": v(-15, -108) * mm, "end": v(-15, -120) * mm});
            skLineSegment(sketch, "E92.MirrorCS", {"start": v(-33, -90) * mm, "end": v(-15, -108) * mm});
            skLineSegment(sketch, "E93.MirrorCS", {"start": v(15, -108) * mm, "end": v(15, -120) * mm});
            skLineSegment(sketch, "E94.MirrorCS", {"start": v(33, -90) * mm, "end": v(15, -108) * mm});
            skSolve(sketch);
        }
        {
            var Q0;
            Q0 = qSketchRegion(id + "F16", true);
            var Q1;
            Q1=makeQuery(id+"F2.opExtrude","CAP_FACE",FACE,{"disambiguationData":[OSD([sQuery(id+"F0.wireOp",EDGE,"E12"),sQuery(id+"F0.wireOp",EDGE,"E13"),sQuery(id+"F0.wireOp",EDGE,"E14"),sQuery(id+"F0.wireOp",EDGE,"E15"),sQuery(id+"F0.wireOp",EDGE,"E17.filletArc"),sQuery(id+"F0.wireOp",EDGE,"E18.filletArc"),sQuery(id+"F0.wireOp",EDGE,"E19.filletArc"),sQuery(id+"F0.wireOp",EDGE,"E20.filletArc"),sQuery(id+"F0.wireOp",EDGE,"E25.0"),sQuery(id+"F0.wireOp",EDGE,"E25.1"),sQuery(id+"F0.wireOp",EDGE,"E25.2"),sQuery(id+"F0.wireOp",EDGE,"E25.3"),sQuery(id+"F0.wireOp",EDGE,"E25.4"),sQuery(id+"F0.wireOp",EDGE,"E25.5"),sQuery(id+"F0.wireOp",EDGE,"E25.6"),sQuery(id+"F0.wireOp",EDGE,"E25.7")])],"isStart":false});
            extrude(context, id + "F17", {"entities" : qUnion([Q0]), "endBound" : BoundingType.UP_TO_SURFACE, "endBoundEntityFace" : qUnion([Q1]), "depth" : 25 * mm});
        }
    });
